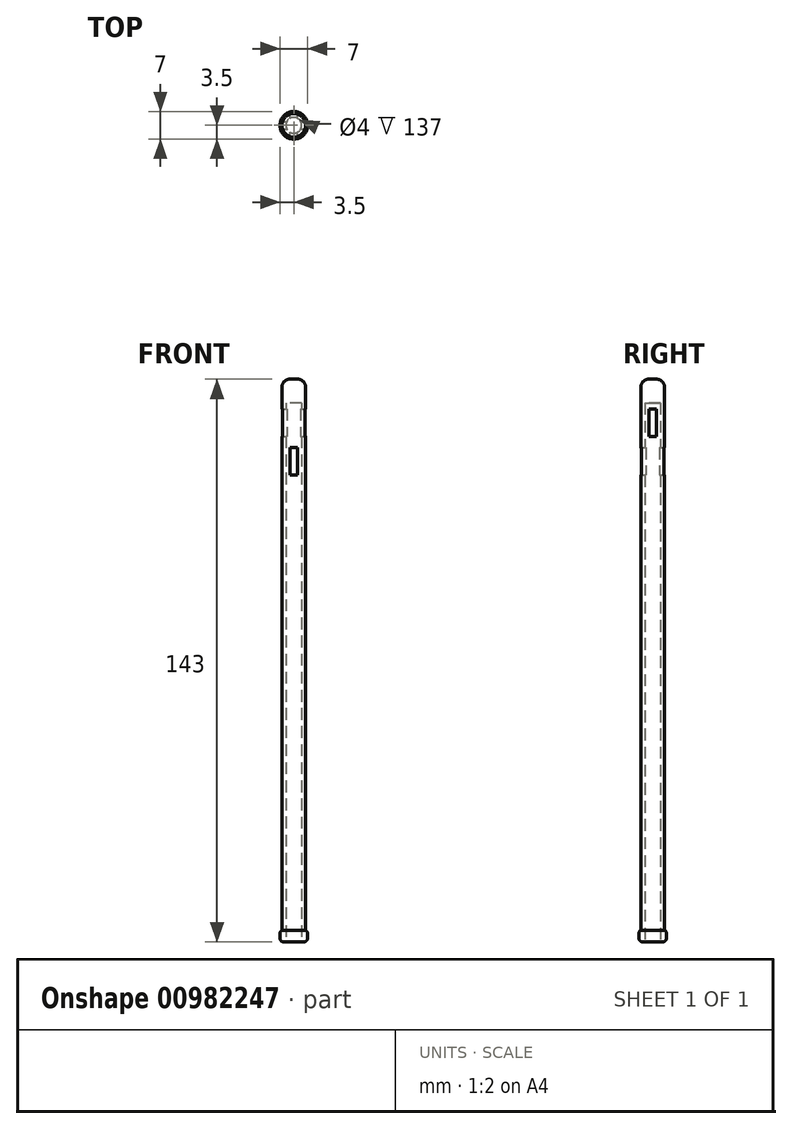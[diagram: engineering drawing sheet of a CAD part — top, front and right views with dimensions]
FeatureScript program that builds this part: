
annotation { "Feature Type Name" : "Feature", "Feature Type Description" : "" }
export const myFeature = defineFeature(function(context is Context, id is Id, definition is map)
    precondition{}
    {
        {
            var Q0;
            Q0=qCreatedBy(makeId("Top.planeOp"),FACE);
            var sketch = newSketch(context, id + "F0", { "sketchPlane" : qUnion([Q0])});
            skCircle(sketch, "E0", {"center": v(0, 0) * mm, "radius": 3 * mm});
            skCircle(sketch, "E1", {"center": v(0, 0) * mm, "radius": 2 * mm});
            skSolve(sketch);
        }
        {
            var Q0;
            Q0=makeQuery(id+"F0.imprint","IMPRINT",FACE,{"disambiguationData":[TD([[makeQuery(id+"F0.imprint","IMPRINT",EDGE,{"derivedFrom":sQuery(id+"F0.wireOp",EDGE,"E0")}),1.0]])]});
            extrude(context, id + "F1", {"entities" : qUnion([Q0]), "depth" : 100 * mm, "offsetDistance" : 25 * mm});
        }
        {
            var Q0;
            Q0=makeQuery(id+"F1.opExtrude","CAP_FACE",FACE,{"disambiguationData":[OSD([sQuery(id+"F0.wireOp",EDGE,"E0"),sQuery(id+"F0.wireOp",EDGE,"E1")])],"isStart":false});
            var sketch = newSketch(context, id + "F2", { "sketchPlane" : qUnion([Q0])});
            skCircle(sketch, "E2", {"center": v(0, 0) * mm, "radius": 3 * mm});
            skSolve(sketch);
        }
        {
            var Q0;
            Q0=makeQuery(id+"F2.imprint","IMPRINT",FACE,{"disambiguationData":[TD([[makeQuery(id+"F2.imprint","IMPRINT",EDGE,{"derivedFrom":sQuery(id+"F2.wireOp",EDGE,"E2")}),1.0]])]});
            var Q1;
            Q1=makeQuery(id+"F2.imprint","IMPRINT",FACE,{"disambiguationData":[TD([[makeQuery(id+"F2.imprint","IMPRINT",EDGE,{"derivedFrom":makeQuery(id+"F1.opExtrude","CAP_EDGE",EDGE,{"disambiguationData":[OSD([sQuery(id+"F0.wireOp",EDGE,"E1")])],"isStart":false})}),1.0]])]});
            extrude(context, id + "F3", {"entities" : qUnion([Q0, Q1]), "operationType" : NewBodyOperationType.ADD, "depth" : 6 * mm, "offsetDistance" : 25 * mm});
        }
        {
            var Q0;
            Q0=qCreatedBy(makeId("Front.planeOp"),FACE);
            var sketch = newSketch(context, id + "F4", { "sketchPlane" : qUnion([Q0])});
            skLineSegment(sketch, "E3.bottom", {"start": v(1, 81.63) * mm, "end": v(-1, 81.63) * mm});
            skLineSegment(sketch, "E3.top", {"start": v(1, 88.63) * mm, "end": v(-1, 88.63) * mm});
            skLineSegment(sketch, "E3.left", {"start": v(1, 81.63) * mm, "end": v(1, 88.63) * mm});
            skLineSegment(sketch, "E3.right", {"start": v(-1, 81.63) * mm, "end": v(-1, 88.63) * mm});
            skPoint(sketch, "E3.middle", {"position": v(0, 85.13) * mm});
            skSolve(sketch);
        }
        {
            var Q0;
            Q0=qCreatedBy(makeId("Right.planeOp"),FACE);
            var sketch = newSketch(context, id + "F5", { "sketchPlane" : qUnion([Q0])});
            skLineSegment(sketch, "E4.bottom", {"start": v(-1, 91.46) * mm, "end": v(1, 91.46) * mm});
            skLineSegment(sketch, "E4.top", {"start": v(-1, 98.46) * mm, "end": v(1, 98.46) * mm});
            skLineSegment(sketch, "E4.left", {"start": v(-1, 91.46) * mm, "end": v(-1, 98.46) * mm});
            skLineSegment(sketch, "E4.right", {"start": v(1, 91.46) * mm, "end": v(1, 98.46) * mm});
            skPoint(sketch, "E4.middle", {"position": v(0, 94.96) * mm});
            skSolve(sketch);
        }
        {
            var Q0;
            Q0 = qSketchRegion(id + "F4", true);
            extrude(context, id + "F6", {"entities" : qUnion([Q0]), "operationType" : NewBodyOperationType.REMOVE, "endBound" : BoundingType.SYMMETRIC, "depth" : 25 * mm, "offsetDistance" : 25 * mm});
        }
        {
            var Q0;
            Q0 = qSketchRegion(id + "F5", true);
            extrude(context, id + "F7", {"entities" : qUnion([Q0]), "operationType" : NewBodyOperationType.REMOVE, "endBound" : BoundingType.SYMMETRIC, "oppositeDirection" : true, "depth" : 25 * mm, "offsetDistance" : 25 * mm});
        }
        {
            var Q0;
            Q0=makeQuery(id+"F3.opExtrude","CAP_FACE",FACE,{"disambiguationData":[OSD([sQuery(id+"F2.wireOp",EDGE,"E2")])],"isStart":false});
            fillet(context, id + "F8", {"entities" : qUnion([Q0]), "radius" : 2 * mm, "tangentPropagation" : true, "allowEdgeOverflow" : false});
        }
        {
            var Q0;
            Q0=makeQuery(id+"F1.opExtrude","CAP_FACE",FACE,{"disambiguationData":[OSD([sQuery(id+"F0.wireOp",EDGE,"E0"),sQuery(id+"F0.wireOp",EDGE,"E1")])],"isStart":true});
            extrude(context, id + "F9", {"entities" : qUnion([Q0]), "operationType" : NewBodyOperationType.ADD, "depth" : 34 * mm, "offsetDistance" : 25 * mm});
        }
        {
            var Q0;
            Q0=makeQuery(id+"F9.opExtrude","CAP_FACE",FACE,{"disambiguationData":[OSD([sQuery(id+"F0.wireOp",EDGE,"E0"),sQuery(id+"F0.wireOp",EDGE,"E1")])],"isStart":false});
            var sketch = newSketch(context, id + "F10", { "sketchPlane" : qUnion([Q0])});
            skCircle(sketch, "E5", {"center": v(0, 0) * mm, "radius": 3.5 * mm});
            skSolve(sketch);
        }
        {
            var Q0;
            Q0=makeQuery(id+"F10.imprint","IMPRINT",FACE,{"disambiguationData":[TD([[makeQuery(id+"F10.imprint","IMPRINT",EDGE,{"derivedFrom":sQuery(id+"F10.wireOp",EDGE,"E5")}),1.0]])]});
            var Q1;
            Q1=makeQuery(id+"F10.imprint","IMPRINT",FACE,{"disambiguationData":[TD([[makeQuery(id+"F10.imprint","IMPRINT",EDGE,{"derivedFrom":makeQuery(id+"F9.opExtrude","CAP_EDGE",EDGE,{"disambiguationData":[OSD([sQuery(id+"F0.wireOp",EDGE,"E0")])],"isStart":false})}),-1.0]])]});
            extrude(context, id + "F11", {"entities" : qUnion([Q0, Q1]), "operationType" : NewBodyOperationType.ADD, "depth" : 3 * mm, "offsetDistance" : 25 * mm});
        }
        {
            var Q0;
            Q0=makeQuery(id+"F11.opExtrude","CAP_EDGE",EDGE,{"disambiguationData":[OSD([sQuery(id+"F10.wireOp",EDGE,"E5")])],"isStart":true});
            var Q1;
            Q1=makeQuery(id+"F11.opExtrude","CAP_EDGE",EDGE,{"disambiguationData":[OSD([sQuery(id+"F10.wireOp",EDGE,"E5")])],"isStart":false});
            fillet(context, id + "F12", {"entities" : qUnion([Q0, Q1]), "radius" : 1 * mm, "tangentPropagation" : true, "allowEdgeOverflow" : false});
        }
    });
